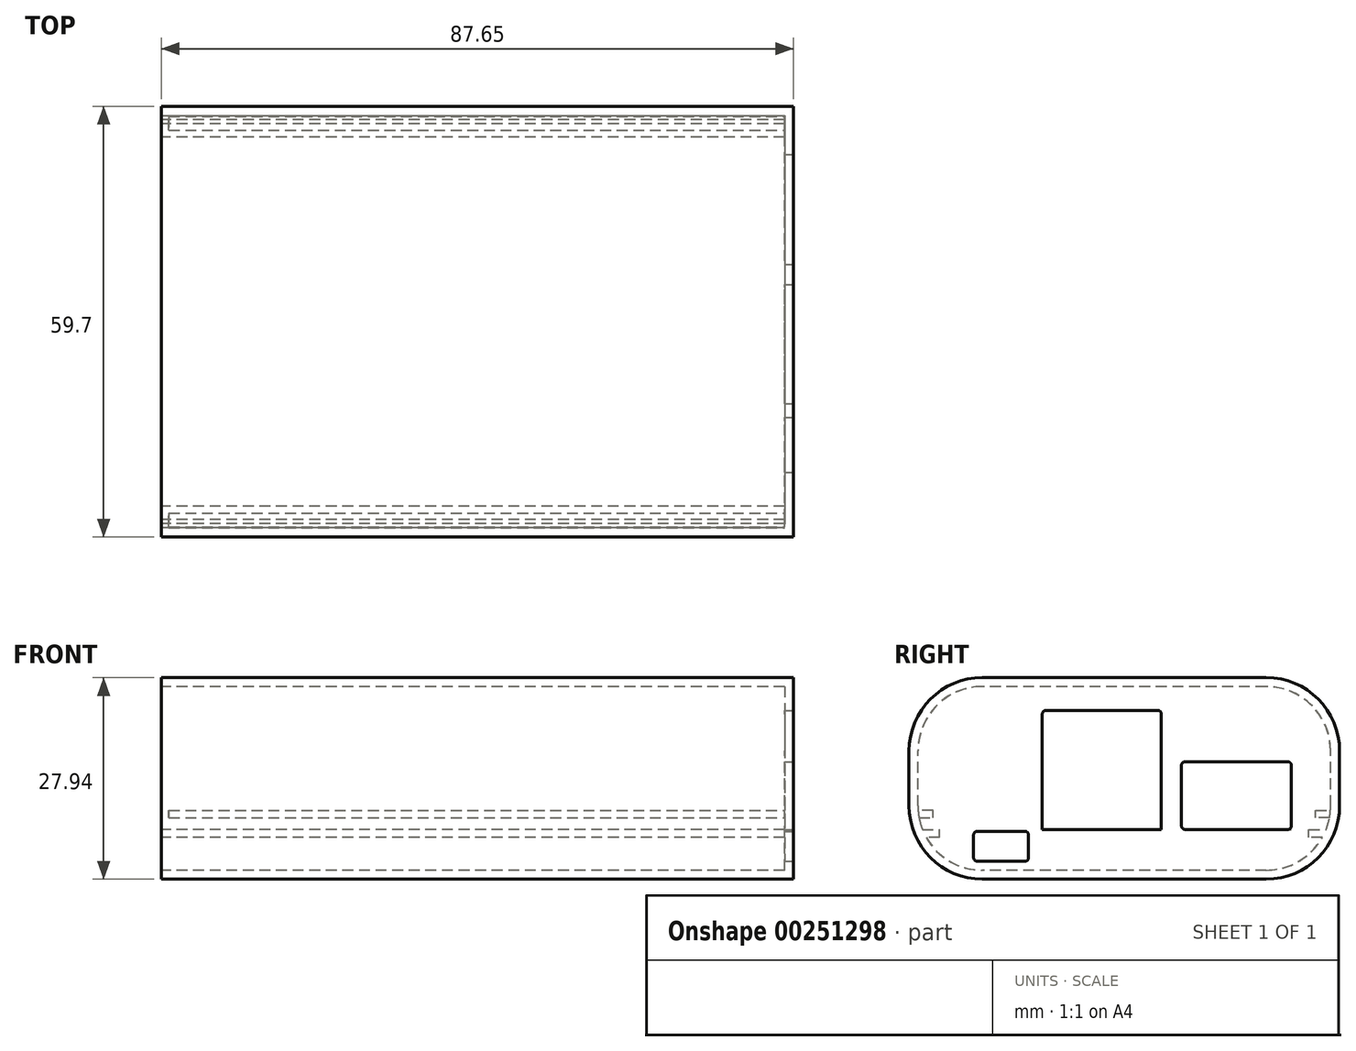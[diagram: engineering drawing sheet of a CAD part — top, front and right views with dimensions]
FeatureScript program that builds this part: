
annotation { "Feature Type Name" : "Feature", "Feature Type Description" : "" }
export const myFeature = defineFeature(function(context is Context, id is Id, definition is map)
    precondition{}
    {
        {
            var Q0;
            Q0=qCreatedBy(makeId("Right.planeOp"),FACE);
            var sketch = newSketch(context, id + "F0", { "sketchPlane" : qUnion([Q0])});
            skLineSegment(sketch, "E0.bottom", {"start": v(19.69, -13.97) * mm, "end": v(-19.69, -13.97) * mm});
            skLineSegment(sketch, "E0.top", {"start": v(19.69, 13.97) * mm, "end": v(-19.69, 13.97) * mm});
            skLineSegment(sketch, "E0.left", {"start": v(29.85, -3.81) * mm, "end": v(29.85, 3.81) * mm});
            skLineSegment(sketch, "E0.right", {"start": v(-29.85, -3.81) * mm, "end": v(-29.85, 3.8) * mm});
            skPoint(sketch, "E0.middle", {"position": v(0, 0) * mm});
            skPoint(sketch, "E1.visualSharp", {"position": v(-29.85, 13.97) * mm});
            skArc(sketch, "E1.filletArc", {"start": v(-19.69, 13.97) * mm, "mid": v(-26.87, 11) * mm, "end": v(-29.85, 3.8) * mm});
            skPoint(sketch, "E2.visualSharp", {"position": v(-29.84, -13.97) * mm});
            skArc(sketch, "E2.filletArc", {"start": v(-29.85, -3.81) * mm, "mid": v(-26.87, -11) * mm, "end": v(-19.69, -13.97) * mm});
            skPoint(sketch, "E3.visualSharp", {"position": v(29.85, -13.97) * mm});
            skArc(sketch, "E3.filletArc", {"start": v(19.69, -13.97) * mm, "mid": v(26.87, -11) * mm, "end": v(29.85, -3.81) * mm});
            skPoint(sketch, "E4.visualSharp", {"position": v(29.85, 13.97) * mm});
            skArc(sketch, "E4.filletArc", {"start": v(29.85, 3.81) * mm, "mid": v(26.87, 11) * mm, "end": v(19.69, 13.97) * mm});
            skSolve(sketch);
        }
        {
            var Q0;
            Q0=makeQuery(id+"F0.imprint","IMPRINT",FACE,{"disambiguationData":[TD([[makeQuery(id+"F0.imprint","IMPRINT",EDGE,{"derivedFrom":sQuery(id+"F0.wireOp",EDGE,"E0.bottom")}),-1.0]])]});
            extrude(context, id + "F1", {"entities" : qUnion([Q0]), "depth" : 44.45 * mm, "hasSecondDirection" : true, "secondDirectionOppositeDirection" : true, "secondDirectionDepth" : 44.45 * mm});
        }
        {
            var Q0;
            Q0=makeQuery(id+"F1.opExtrude","CAP_FACE",FACE,{"disambiguationData":[OSD([sQuery(id+"F0.wireOp",EDGE,"E0.bottom"),sQuery(id+"F0.wireOp",EDGE,"E0.top"),sQuery(id+"F0.wireOp",EDGE,"E0.left"),sQuery(id+"F0.wireOp",EDGE,"E0.right"),sQuery(id+"F0.wireOp",EDGE,"E1.filletArc"),sQuery(id+"F0.wireOp",EDGE,"E2.filletArc"),sQuery(id+"F0.wireOp",EDGE,"E3.filletArc"),sQuery(id+"F0.wireOp",EDGE,"E4.filletArc")])],"isStart":false});
            var Q1;
            Q1=makeQuery(id+"F1.opExtrude","SWEPT_BODY",BODY,{"disambiguationData":[OSD([sQuery(id+"F0.wireOp",EDGE,"E0.bottom"),sQuery(id+"F0.wireOp",EDGE,"E0.top"),sQuery(id+"F0.wireOp",EDGE,"E0.left"),sQuery(id+"F0.wireOp",EDGE,"E0.right"),sQuery(id+"F0.wireOp",EDGE,"E1.filletArc"),sQuery(id+"F0.wireOp",EDGE,"E2.filletArc"),sQuery(id+"F0.wireOp",EDGE,"E3.filletArc"),sQuery(id+"F0.wireOp",EDGE,"E4.filletArc")])]});
            shell(context, id + "F2", {"isHollow" : true, "entities" : qUnion([Q0]), "parts" : qUnion([Q1]), "thickness" : 1.24 * mm});
        }
        {
            var Q0;
            Q0=makeQuery(id+"F1.opExtrude","CAP_FACE",FACE,{"disambiguationData":[OSD([sQuery(id+"F0.wireOp",EDGE,"E0.bottom"),sQuery(id+"F0.wireOp",EDGE,"E0.top"),sQuery(id+"F0.wireOp",EDGE,"E0.left"),sQuery(id+"F0.wireOp",EDGE,"E0.right"),sQuery(id+"F0.wireOp",EDGE,"E1.filletArc"),sQuery(id+"F0.wireOp",EDGE,"E2.filletArc"),sQuery(id+"F0.wireOp",EDGE,"E3.filletArc"),sQuery(id+"F0.wireOp",EDGE,"E4.filletArc")])],"isStart":false});
            var sketch = newSketch(context, id + "F3", { "sketchPlane" : qUnion([Q0])});
            skLineSegment(sketch, "E5", {"start": v(-29.3, -7.09) * mm, "end": v(29.3, -7.09) * mm});
            skLineSegment(sketch, "E6", {"start": v(29.3, -7.09) * mm, "end": v(28.86, -8.18) * mm});
            skLineSegment(sketch, "E7", {"start": v(28.86, -8.18) * mm, "end": v(-28.86, -8.18) * mm});
            skLineSegment(sketch, "E8", {"start": v(-28.86, -8.18) * mm, "end": v(-29.3, -7.09) * mm});
            skSolve(sketch);
        }
        {
            var Q0;
            Q0=makeQuery(id+"F3.imprint","IMPRINT",FACE,{"disambiguationData":[TD([[makeQuery(id+"F3.imprint","IMPRINT",EDGE,{"derivedFrom":sQuery(id+"F3.wireOp",EDGE,"E5")}),-1.0]])]});
            extrude(context, id + "F4", {"entities" : qUnion([Q0]), "operationType" : NewBodyOperationType.ADD, "oppositeDirection" : true, "depth" : 89.36 * mm});
        }
        {
            var Q0;
            Q0=makeQuery(id+"F4.opExtrude","CAP_FACE",FACE,{"disambiguationData":[OSD([sQuery(id+"F3.wireOp",EDGE,"E5"),sQuery(id+"F3.wireOp",EDGE,"E6"),sQuery(id+"F3.wireOp",EDGE,"E7"),sQuery(id+"F3.wireOp",EDGE,"E8")])],"isStart":false});
            var sketch = newSketch(context, id + "F5", { "sketchPlane" : qUnion([Q0])});
            skLineSegment(sketch, "E9", {"start": v(-25.59, -7.09) * mm, "end": v(-25.59, -8.18) * mm});
            skLineSegment(sketch, "E10.MirrorCS", {"start": v(25.59, -7.09) * mm, "end": v(25.59, -8.18) * mm});
            skSolve(sketch);
        }
        {
            var Q0;
            {var subQ0=sQuery(id+"F5.wireOp",EDGE,"E9");Q0=makeQuery(id+"F5.imprint","IMPRINT",FACE,{"disambiguationData":[TD([[makeQuery(id+"F5.imprint","IMPRINT",EDGE,{"derivedFrom":subQ0}),1.0]])]});}
            extrude(context, id + "F6", {"entities" : qUnion([Q0]), "operationType" : NewBodyOperationType.REMOVE, "oppositeDirection" : true, "depth" : 89.4 * mm});
        }
        {
            var Q0;
            Q0=makeQuery(id+"F1.opExtrude","CAP_FACE",FACE,{"disambiguationData":[OSD([sQuery(id+"F0.wireOp",EDGE,"E0.bottom"),sQuery(id+"F0.wireOp",EDGE,"E0.top"),sQuery(id+"F0.wireOp",EDGE,"E0.left"),sQuery(id+"F0.wireOp",EDGE,"E0.right"),sQuery(id+"F0.wireOp",EDGE,"E1.filletArc"),sQuery(id+"F0.wireOp",EDGE,"E2.filletArc"),sQuery(id+"F0.wireOp",EDGE,"E3.filletArc"),sQuery(id+"F0.wireOp",EDGE,"E4.filletArc")])],"isStart":false});
            var sketch = newSketch(context, id + "F7", { "sketchPlane" : qUnion([Q0])});
            skLineSegment(sketch, "E11", {"start": v(-11.36, -7.09) * mm, "end": v(-11.36, 9.42) * mm});
            skLineSegment(sketch, "E12", {"start": v(-11.36, 9.42) * mm, "end": v(5.15, 9.42) * mm});
            skLineSegment(sketch, "E13", {"start": v(5.15, 9.42) * mm, "end": v(5.15, -7.09) * mm});
            skLineSegment(sketch, "E14", {"start": v(7.93, -7.09) * mm, "end": v(7.93, 2.31) * mm});
            skLineSegment(sketch, "E15", {"start": v(7.93, 2.31) * mm, "end": v(23.17, 2.31) * mm});
            skLineSegment(sketch, "E16", {"start": v(23.17, 2.31) * mm, "end": v(23.17, -7.09) * mm});
            skSolve(sketch);
        }
        {
            var Q0;
            {var subQ0=sQuery(id+"F7.wireOp",EDGE,"E11");Q0=makeQuery(id+"F7.imprint","IMPRINT",FACE,{"disambiguationData":[TD([[makeQuery(id+"F7.imprint","IMPRINT",EDGE,{"derivedFrom":subQ0}),-1.0]])]});}
            var Q1;
            {var subQ0=sQuery(id+"F7.wireOp",EDGE,"E14");Q1=makeQuery(id+"F7.imprint","IMPRINT",FACE,{"disambiguationData":[TD([[makeQuery(id+"F7.imprint","IMPRINT",EDGE,{"derivedFrom":subQ0}),-1.0]])]});}
            extrude(context, id + "F8", {"entities" : qUnion([Q0, Q1]), "operationType" : NewBodyOperationType.REMOVE, "oppositeDirection" : true, "depth" : 25.4 * mm});
        }
        {
            var Q0;
            Q0=makeQuery(id+"F1.opExtrude","CAP_FACE",FACE,{"disambiguationData":[OSD([sQuery(id+"F0.wireOp",EDGE,"E0.bottom"),sQuery(id+"F0.wireOp",EDGE,"E0.top"),sQuery(id+"F0.wireOp",EDGE,"E0.left"),sQuery(id+"F0.wireOp",EDGE,"E0.right"),sQuery(id+"F0.wireOp",EDGE,"E1.filletArc"),sQuery(id+"F0.wireOp",EDGE,"E2.filletArc"),sQuery(id+"F0.wireOp",EDGE,"E3.filletArc"),sQuery(id+"F0.wireOp",EDGE,"E4.filletArc")])],"isStart":false});
            var sketch = newSketch(context, id + "F9", { "sketchPlane" : qUnion([Q0])});
            skLineSegment(sketch, "E17", {"start": v(-13.27, -8.18) * mm, "end": v(-13.27, -11.48) * mm});
            skLineSegment(sketch, "E18", {"start": v(-13.27, -11.48) * mm, "end": v(-20.89, -11.48) * mm});
            skLineSegment(sketch, "E19", {"start": v(-20.89, -11.48) * mm, "end": v(-20.89, -8.18) * mm});
            skSolve(sketch);
        }
        {
            var Q0;
            {var subQ0=sQuery(id+"F9.wireOp",EDGE,"E17");Q0=makeQuery(id+"F9.imprint","IMPRINT",FACE,{"disambiguationData":[TD([[makeQuery(id+"F9.imprint","IMPRINT",EDGE,{"derivedFrom":subQ0}),-1.0]])]});}
            extrude(context, id + "F10", {"entities" : qUnion([Q0]), "operationType" : NewBodyOperationType.REMOVE, "oppositeDirection" : true, "depth" : 25.4 * mm});
        }
        {
            var Q0;
            Q0=makeQuery(id+"F1.opExtrude","CAP_FACE",FACE,{"disambiguationData":[OSD([sQuery(id+"F0.wireOp",EDGE,"E0.bottom"),sQuery(id+"F0.wireOp",EDGE,"E0.top"),sQuery(id+"F0.wireOp",EDGE,"E0.left"),sQuery(id+"F0.wireOp",EDGE,"E0.right"),sQuery(id+"F0.wireOp",EDGE,"E1.filletArc"),sQuery(id+"F0.wireOp",EDGE,"E2.filletArc"),sQuery(id+"F0.wireOp",EDGE,"E3.filletArc"),sQuery(id+"F0.wireOp",EDGE,"E4.filletArc")])],"isStart":false});
            var sketch = newSketch(context, id + "F11", { "sketchPlane" : qUnion([Q0])});
            skLineSegment(sketch, "E20", {"start": v(-11.36, -7.09) * mm, "end": v(5.15, -7.09) * mm});
            skLineSegment(sketch, "E21", {"start": v(5.15, -7.09) * mm, "end": v(7.93, -7.09) * mm});
            skLineSegment(sketch, "E22", {"start": v(7.93, -7.09) * mm, "end": v(23.17, -7.09) * mm});
            skLineSegment(sketch, "E23", {"start": v(-20.89, -8.18) * mm, "end": v(-13.27, -8.18) * mm});
            skSolve(sketch);
        }
        {
            var Q0;
            Q0=makeQuery(id+"F11.imprint","IMPRINT",FACE,{"disambiguationData":[TD([[makeQuery(id+"F11.imprint","IMPRINT",EDGE,{"derivedFrom":sQuery(id+"F11.wireOp",EDGE,"E20")}),-1.0]])]});
            extrude(context, id + "F12", {"entities" : qUnion([Q0]), "operationType" : NewBodyOperationType.ADD, "oppositeDirection" : true, "depth" : 1.25 * mm});
        }
        {
            var Q0;
            {var subQ0=sQuery(id+"F0.wireOp",EDGE,"E4.filletArc");var subQ1=sQuery(id+"F0.wireOp",EDGE,"E2.filletArc");var subQ2=sQuery(id+"F0.wireOp",EDGE,"E1.filletArc");var subQ3=sQuery(id+"F0.wireOp",EDGE,"E3.filletArc");var subQ4=sQuery(id+"F0.wireOp",EDGE,"E0.right");var subQ5=sQuery(id+"F0.wireOp",EDGE,"E0.left");var subQ6=sQuery(id+"F0.wireOp",EDGE,"E0.top");var subQ7=makeQuery(id+"F1.opExtrude","CAP_FACE",FACE,{"disambiguationData":[OSD([sQuery(id+"F0.wireOp",EDGE,"E0.bottom"),subQ6,subQ5,subQ4,subQ2,subQ1,subQ3,subQ0])],"isStart":true});Q0=makeQuery(id+"F4.boolean.opBoolean","SPLIT",FACE,{"disambiguationData":[TD([subQ7,makeQuery(id+"F1.opExtrude","SWEPT_FACE",FACE,{"disambiguationData":[OSD([subQ6])]}),makeQuery(id+"F1.opExtrude","SWEPT_FACE",FACE,{"disambiguationData":[OSD([subQ5])]}),makeQuery(id+"F1.opExtrude","SWEPT_FACE",FACE,{"disambiguationData":[OSD([subQ4])]}),makeQuery(id+"F1.opExtrude","SWEPT_FACE",FACE,{"disambiguationData":[OSD([subQ2])]}),makeQuery(id+"F1.opExtrude","SWEPT_FACE",FACE,{"disambiguationData":[OSD([subQ1])]}),makeQuery(id+"F1.opExtrude","SWEPT_FACE",FACE,{"disambiguationData":[OSD([subQ3])]}),makeQuery(id+"F1.opExtrude","SWEPT_FACE",FACE,{"disambiguationData":[OSD([subQ0])]}),makeQuery(id+"F4.opExtrude","SWEPT_FACE",FACE,{"disambiguationData":[OSD([sQuery(id+"F3.wireOp",EDGE,"E5")])]}),makeQuery(id+"F4.opExtrude","SWEPT_FACE",FACE,{"disambiguationData":[OSD([sQuery(id+"F3.wireOp",EDGE,"E6")])]}),makeQuery(id+"F4.opExtrude","SWEPT_FACE",FACE,{"disambiguationData":[OSD([sQuery(id+"F3.wireOp",EDGE,"E8")])]})])],"derivedFrom":subQ7});}
            var Q1;
            {var subQ0=sQuery(id+"F0.wireOp",EDGE,"E3.filletArc");var subQ1=sQuery(id+"F0.wireOp",EDGE,"E2.filletArc");var subQ2=sQuery(id+"F0.wireOp",EDGE,"E0.bottom");var subQ3=makeQuery(id+"F1.opExtrude","CAP_FACE",FACE,{"disambiguationData":[OSD([subQ2,sQuery(id+"F0.wireOp",EDGE,"E0.top"),sQuery(id+"F0.wireOp",EDGE,"E0.left"),sQuery(id+"F0.wireOp",EDGE,"E0.right"),sQuery(id+"F0.wireOp",EDGE,"E1.filletArc"),subQ1,subQ0,sQuery(id+"F0.wireOp",EDGE,"E4.filletArc")])],"isStart":true});Q1=makeQuery(id+"F4.boolean.opBoolean","SPLIT",FACE,{"disambiguationData":[TD([makeQuery(id+"F1.opExtrude","SWEPT_FACE",FACE,{"disambiguationData":[OSD([subQ2])]}),subQ3,makeQuery(id+"F1.opExtrude","SWEPT_FACE",FACE,{"disambiguationData":[OSD([subQ1])]}),makeQuery(id+"F1.opExtrude","SWEPT_FACE",FACE,{"disambiguationData":[OSD([subQ0])]}),makeQuery(id+"F4.opExtrude","SWEPT_FACE",FACE,{"disambiguationData":[OSD([sQuery(id+"F3.wireOp",EDGE,"E6")])]}),makeQuery(id+"F4.opExtrude","SWEPT_FACE",FACE,{"disambiguationData":[OSD([sQuery(id+"F3.wireOp",EDGE,"E7")])]}),makeQuery(id+"F4.opExtrude","SWEPT_FACE",FACE,{"disambiguationData":[OSD([sQuery(id+"F3.wireOp",EDGE,"E8")])]})])],"derivedFrom":subQ3});}
            extrude(context, id + "F13", {"entities" : qUnion([Q0, Q1]), "operationType" : NewBodyOperationType.REMOVE, "oppositeDirection" : true, "depth" : 1.25 * mm});
        }
        {
            var Q0;
            {var subQ0=sQuery(id+"F3.wireOp",EDGE,"E5");var subQ1=sQuery(id+"F3.wireOp",EDGE,"E6");var subQ2=sQuery(id+"F3.wireOp",EDGE,"E7");Q0=makeQuery(id+"F6.boolean.opBoolean","SPLIT",FACE,{"disambiguationData":[TD([makeQuery(id+"F4.opExtrude","SWEPT_FACE",FACE,{"disambiguationData":[OSD([subQ1])]})])],"derivedFrom":makeQuery(id+"F4.opExtrude","CAP_FACE",FACE,{"disambiguationData":[OSD([subQ0,subQ1,subQ2,sQuery(id+"F3.wireOp",EDGE,"E8")])],"isStart":false})});}
            var Q1;
            {var subQ0=sQuery(id+"F3.wireOp",EDGE,"E5");var subQ1=sQuery(id+"F3.wireOp",EDGE,"E8");var subQ2=sQuery(id+"F3.wireOp",EDGE,"E7");Q1=makeQuery(id+"F6.boolean.opBoolean","SPLIT",FACE,{"disambiguationData":[TD([makeQuery(id+"F4.opExtrude","SWEPT_FACE",FACE,{"disambiguationData":[OSD([subQ1])]})])],"derivedFrom":makeQuery(id+"F4.opExtrude","CAP_FACE",FACE,{"disambiguationData":[OSD([subQ0,sQuery(id+"F3.wireOp",EDGE,"E6"),subQ2,subQ1])],"isStart":false})});}
            var Q2;
            {var subQ0=sQuery(id+"F0.wireOp",EDGE,"E2.filletArc");var subQ1=makeQuery(id+"F1.opExtrude","CAP_FACE",FACE,{"disambiguationData":[OSD([sQuery(id+"F0.wireOp",EDGE,"E0.bottom"),sQuery(id+"F0.wireOp",EDGE,"E0.top"),sQuery(id+"F0.wireOp",EDGE,"E0.left"),sQuery(id+"F0.wireOp",EDGE,"E0.right"),sQuery(id+"F0.wireOp",EDGE,"E1.filletArc"),subQ0,sQuery(id+"F0.wireOp",EDGE,"E3.filletArc"),sQuery(id+"F0.wireOp",EDGE,"E4.filletArc")])],"isStart":true});Q2=makeQuery(id+"F4.boolean.opBoolean","SPLIT",FACE,{"disambiguationData":[TD([subQ1,makeQuery(id+"F1.opExtrude","SWEPT_FACE",FACE,{"disambiguationData":[OSD([subQ0])]}),makeQuery(id+"F4.opExtrude","SWEPT_FACE",FACE,{"disambiguationData":[OSD([sQuery(id+"F3.wireOp",EDGE,"E5")])]}),makeQuery(id+"F4.opExtrude","SWEPT_FACE",FACE,{"disambiguationData":[OSD([sQuery(id+"F3.wireOp",EDGE,"E7")])]}),makeQuery(id+"F4.opExtrude","SWEPT_FACE",FACE,{"disambiguationData":[OSD([sQuery(id+"F3.wireOp",EDGE,"E8")])]})])],"derivedFrom":subQ1});}
            var Q3;
            {var subQ0=sQuery(id+"F0.wireOp",EDGE,"E3.filletArc");var subQ1=makeQuery(id+"F1.opExtrude","CAP_FACE",FACE,{"disambiguationData":[OSD([sQuery(id+"F0.wireOp",EDGE,"E0.bottom"),sQuery(id+"F0.wireOp",EDGE,"E0.top"),sQuery(id+"F0.wireOp",EDGE,"E0.left"),sQuery(id+"F0.wireOp",EDGE,"E0.right"),sQuery(id+"F0.wireOp",EDGE,"E1.filletArc"),sQuery(id+"F0.wireOp",EDGE,"E2.filletArc"),subQ0,sQuery(id+"F0.wireOp",EDGE,"E4.filletArc")])],"isStart":true});Q3=makeQuery(id+"F4.boolean.opBoolean","SPLIT",FACE,{"disambiguationData":[TD([subQ1,makeQuery(id+"F1.opExtrude","SWEPT_FACE",FACE,{"disambiguationData":[OSD([subQ0])]}),makeQuery(id+"F4.opExtrude","SWEPT_FACE",FACE,{"disambiguationData":[OSD([sQuery(id+"F3.wireOp",EDGE,"E5")])]}),makeQuery(id+"F4.opExtrude","SWEPT_FACE",FACE,{"disambiguationData":[OSD([sQuery(id+"F3.wireOp",EDGE,"E6")])]}),makeQuery(id+"F4.opExtrude","SWEPT_FACE",FACE,{"disambiguationData":[OSD([sQuery(id+"F3.wireOp",EDGE,"E7")])]})])],"derivedFrom":subQ1});}
            extrude(context, id + "F14", {"entities" : qUnion([Q0, Q1, Q2, Q3]), "operationType" : NewBodyOperationType.REMOVE, "oppositeDirection" : true, "depth" : 1.7 * mm});
        }
        {
            var Q0;
            {var subQ0=sQuery(id+"F0.wireOp",EDGE,"E3.filletArc");var subQ1=sQuery(id+"F0.wireOp",EDGE,"E4.filletArc");var subQ2=sQuery(id+"F0.wireOp",EDGE,"E2.filletArc");var subQ3=sQuery(id+"F0.wireOp",EDGE,"E1.filletArc");var subQ4=sQuery(id+"F0.wireOp",EDGE,"E0.right");var subQ5=sQuery(id+"F0.wireOp",EDGE,"E0.left");var subQ6=sQuery(id+"F0.wireOp",EDGE,"E0.top");var subQ7=sQuery(id+"F0.wireOp",EDGE,"E0.bottom");var subQ8=makeQuery(id+"F1.opExtrude","CAP_FACE",FACE,{"disambiguationData":[OSD([subQ7,subQ6,subQ5,subQ4,subQ3,subQ2,subQ0,subQ1])],"isStart":true});Q0=makeQuery(id+"F14.boolean.opBoolean","COPY",FACE,{"derivedFrom":makeQuery(id+"F14.opExtrude","CAP_FACE",FACE,{"disambiguationData":[OSD([subQ7,subQ6,subQ5,subQ4,subQ3,subQ2,subQ0,subQ1]),TDD([makeQuery(id+"F4.boolean.opBoolean","SPLIT",FACE,{"disambiguationData":[TD([subQ8,makeQuery(id+"F1.opExtrude","SWEPT_FACE",FACE,{"disambiguationData":[OSD([subQ0])]}),makeQuery(id+"F4.opExtrude","SWEPT_FACE",FACE,{"disambiguationData":[OSD([sQuery(id+"F3.wireOp",EDGE,"E5")])]}),makeQuery(id+"F4.opExtrude","SWEPT_FACE",FACE,{"disambiguationData":[OSD([sQuery(id+"F3.wireOp",EDGE,"E6")])]}),makeQuery(id+"F4.opExtrude","SWEPT_FACE",FACE,{"disambiguationData":[OSD([sQuery(id+"F3.wireOp",EDGE,"E7")])]})])],"derivedFrom":subQ8})])],"isStart":false})});}
            var Q1;
            {var subQ0=sQuery(id+"F0.wireOp",EDGE,"E2.filletArc");var subQ1=sQuery(id+"F0.wireOp",EDGE,"E4.filletArc");var subQ2=sQuery(id+"F0.wireOp",EDGE,"E3.filletArc");var subQ3=sQuery(id+"F0.wireOp",EDGE,"E1.filletArc");var subQ4=sQuery(id+"F0.wireOp",EDGE,"E0.right");var subQ5=sQuery(id+"F0.wireOp",EDGE,"E0.left");var subQ6=sQuery(id+"F0.wireOp",EDGE,"E0.top");var subQ7=sQuery(id+"F0.wireOp",EDGE,"E0.bottom");var subQ8=makeQuery(id+"F1.opExtrude","CAP_FACE",FACE,{"disambiguationData":[OSD([subQ7,subQ6,subQ5,subQ4,subQ3,subQ0,subQ2,subQ1])],"isStart":true});Q1=makeQuery(id+"F14.boolean.opBoolean","COPY",FACE,{"derivedFrom":makeQuery(id+"F14.opExtrude","CAP_FACE",FACE,{"disambiguationData":[OSD([subQ7,subQ6,subQ5,subQ4,subQ3,subQ0,subQ2,subQ1]),TDD([makeQuery(id+"F4.boolean.opBoolean","SPLIT",FACE,{"disambiguationData":[TD([subQ8,makeQuery(id+"F1.opExtrude","SWEPT_FACE",FACE,{"disambiguationData":[OSD([subQ0])]}),makeQuery(id+"F4.opExtrude","SWEPT_FACE",FACE,{"disambiguationData":[OSD([sQuery(id+"F3.wireOp",EDGE,"E5")])]}),makeQuery(id+"F4.opExtrude","SWEPT_FACE",FACE,{"disambiguationData":[OSD([sQuery(id+"F3.wireOp",EDGE,"E7")])]}),makeQuery(id+"F4.opExtrude","SWEPT_FACE",FACE,{"disambiguationData":[OSD([sQuery(id+"F3.wireOp",EDGE,"E8")])]})])],"derivedFrom":subQ8})])],"isStart":false})});}
            extrude(context, id + "F15", {"entities" : qUnion([Q0, Q1]), "operationType" : NewBodyOperationType.ADD, "depth" : 0.46 * mm});
        }
        {
            var Q0;
            {var subQ0=sQuery(id+"F0.wireOp",EDGE,"E4.filletArc");var subQ1=sQuery(id+"F0.wireOp",EDGE,"E3.filletArc");var subQ2=sQuery(id+"F0.wireOp",EDGE,"E2.filletArc");var subQ3=sQuery(id+"F0.wireOp",EDGE,"E1.filletArc");var subQ4=sQuery(id+"F0.wireOp",EDGE,"E0.right");var subQ5=sQuery(id+"F0.wireOp",EDGE,"E0.left");var subQ6=sQuery(id+"F0.wireOp",EDGE,"E0.top");var subQ7=sQuery(id+"F0.wireOp",EDGE,"E0.bottom");Q0=makeQuery(id+"F12.boolean.opBoolean","MERGE",FACE,{"derivedFrom":[makeQuery(id+"F1.opExtrude","CAP_FACE",FACE,{"disambiguationData":[OSD([subQ7,subQ6,subQ5,subQ4,subQ3,subQ2,subQ1,subQ0])],"isStart":false}),makeQuery(id+"F12.opExtrude","CAP_FACE",FACE,{"disambiguationData":[OSD([subQ7,subQ6,subQ5,subQ4,subQ3,subQ2,subQ1,subQ0,sQuery(id+"F3.wireOp",EDGE,"E5"),sQuery(id+"F3.wireOp",EDGE,"E7"),sQuery(id+"F5.wireOp",EDGE,"E9"),sQuery(id+"F5.wireOp",EDGE,"E10.MirrorCS"),sQuery(id+"F11.wireOp",EDGE,"E20"),sQuery(id+"F11.wireOp",EDGE,"E21"),sQuery(id+"F11.wireOp",EDGE,"E22"),sQuery(id+"F11.wireOp",EDGE,"E23")])],"isStart":true})]});}
            var sketch = newSketch(context, id + "F16", { "sketchPlane" : qUnion([Q0])});
            skLineSegment(sketch, "E24", {"start": v(-20.89, -8.18) * mm, "end": v(-20.89, -7.34) * mm});
            skLineSegment(sketch, "E25", {"start": v(-20.89, -7.34) * mm, "end": v(-13.27, -7.34) * mm});
            skLineSegment(sketch, "E26", {"start": v(-13.27, -7.34) * mm, "end": v(-13.27, -8.18) * mm});
            skLineSegment(sketch, "E27", {"start": v(-13.27, -8.18) * mm, "end": v(-20.89, -8.18) * mm});
            skSolve(sketch);
        }
        {
            var Q0;
            Q0=makeQuery(id+"F16.imprint","IMPRINT",FACE,{"disambiguationData":[TD([[makeQuery(id+"F16.imprint","IMPRINT",EDGE,{"derivedFrom":sQuery(id+"F16.wireOp",EDGE,"E24")}),-1.0]])]});
            extrude(context, id + "F17", {"entities" : qUnion([Q0]), "operationType" : NewBodyOperationType.REMOVE, "oppositeDirection" : true, "depth" : 25.4 * mm});
        }
        {
            var Q0;
            Q0=makeQuery(id+"F10.boolean.opBoolean","COPY",EDGE,{"derivedFrom":makeQuery(id+"F10.opExtrude","SWEPT_EDGE",EDGE,{"disambiguationData":[OSD([sQuery(id+"F9.wireOp",EDGE,"E17"),sQuery(id+"F9.wireOp",EDGE,"E18")])]})});
            var Q1;
            Q1=makeQuery(id+"F10.boolean.opBoolean","COPY",EDGE,{"derivedFrom":makeQuery(id+"F10.opExtrude","SWEPT_EDGE",EDGE,{"disambiguationData":[OSD([sQuery(id+"F9.wireOp",EDGE,"E18"),sQuery(id+"F9.wireOp",EDGE,"E19")])]})});
            var Q2;
            Q2=makeQuery(id+"F10.boolean.opBoolean","COPY",EDGE,{"derivedFrom":makeQuery(id+"F10.opExtrude","SWEPT_EDGE",EDGE,{"disambiguationData":[OSD([sQuery(id+"F0.wireOp",EDGE,"E0.bottom"),sQuery(id+"F0.wireOp",EDGE,"E0.top"),sQuery(id+"F0.wireOp",EDGE,"E0.left"),sQuery(id+"F0.wireOp",EDGE,"E0.right"),sQuery(id+"F0.wireOp",EDGE,"E1.filletArc"),sQuery(id+"F0.wireOp",EDGE,"E2.filletArc"),sQuery(id+"F0.wireOp",EDGE,"E3.filletArc"),sQuery(id+"F0.wireOp",EDGE,"E4.filletArc"),sQuery(id+"F3.wireOp",EDGE,"E7"),sQuery(id+"F9.wireOp",EDGE,"E17")])]})});
            var Q3;
            Q3=makeQuery(id+"F10.boolean.opBoolean","COPY",EDGE,{"derivedFrom":makeQuery(id+"F10.opExtrude","SWEPT_EDGE",EDGE,{"disambiguationData":[OSD([sQuery(id+"F0.wireOp",EDGE,"E0.bottom"),sQuery(id+"F0.wireOp",EDGE,"E0.top"),sQuery(id+"F0.wireOp",EDGE,"E0.left"),sQuery(id+"F0.wireOp",EDGE,"E0.right"),sQuery(id+"F0.wireOp",EDGE,"E1.filletArc"),sQuery(id+"F0.wireOp",EDGE,"E2.filletArc"),sQuery(id+"F0.wireOp",EDGE,"E3.filletArc"),sQuery(id+"F0.wireOp",EDGE,"E4.filletArc"),sQuery(id+"F3.wireOp",EDGE,"E7"),sQuery(id+"F9.wireOp",EDGE,"E19")])]})});
            var Q4;
            Q4=makeQuery(id+"F8.boolean.opBoolean","COPY",EDGE,{"derivedFrom":makeQuery(id+"F8.opExtrude","SWEPT_EDGE",EDGE,{"disambiguationData":[OSD([sQuery(id+"F7.wireOp",EDGE,"E12"),sQuery(id+"F7.wireOp",EDGE,"E13")])]})});
            var Q5;
            Q5=makeQuery(id+"F8.boolean.opBoolean","COPY",EDGE,{"derivedFrom":makeQuery(id+"F8.opExtrude","SWEPT_EDGE",EDGE,{"disambiguationData":[OSD([sQuery(id+"F7.wireOp",EDGE,"E11"),sQuery(id+"F7.wireOp",EDGE,"E12")])]})});
            var Q6;
            Q6=makeQuery(id+"F8.boolean.opBoolean","COPY",EDGE,{"derivedFrom":makeQuery(id+"F8.opExtrude","SWEPT_EDGE",EDGE,{"disambiguationData":[OSD([sQuery(id+"F0.wireOp",EDGE,"E0.bottom"),sQuery(id+"F0.wireOp",EDGE,"E0.top"),sQuery(id+"F0.wireOp",EDGE,"E0.left"),sQuery(id+"F0.wireOp",EDGE,"E0.right"),sQuery(id+"F0.wireOp",EDGE,"E1.filletArc"),sQuery(id+"F0.wireOp",EDGE,"E2.filletArc"),sQuery(id+"F0.wireOp",EDGE,"E3.filletArc"),sQuery(id+"F0.wireOp",EDGE,"E4.filletArc"),sQuery(id+"F3.wireOp",EDGE,"E5"),sQuery(id+"F7.wireOp",EDGE,"E13")])]})});
            var Q7;
            Q7=makeQuery(id+"F8.boolean.opBoolean","COPY",EDGE,{"derivedFrom":makeQuery(id+"F8.opExtrude","SWEPT_EDGE",EDGE,{"disambiguationData":[OSD([sQuery(id+"F0.wireOp",EDGE,"E0.bottom"),sQuery(id+"F0.wireOp",EDGE,"E0.top"),sQuery(id+"F0.wireOp",EDGE,"E0.left"),sQuery(id+"F0.wireOp",EDGE,"E0.right"),sQuery(id+"F0.wireOp",EDGE,"E1.filletArc"),sQuery(id+"F0.wireOp",EDGE,"E2.filletArc"),sQuery(id+"F0.wireOp",EDGE,"E3.filletArc"),sQuery(id+"F0.wireOp",EDGE,"E4.filletArc"),sQuery(id+"F3.wireOp",EDGE,"E5"),sQuery(id+"F7.wireOp",EDGE,"E11")])]})});
            var Q8;
            Q8=makeQuery(id+"F8.boolean.opBoolean","COPY",EDGE,{"derivedFrom":makeQuery(id+"F8.opExtrude","SWEPT_EDGE",EDGE,{"disambiguationData":[OSD([sQuery(id+"F0.wireOp",EDGE,"E0.bottom"),sQuery(id+"F0.wireOp",EDGE,"E0.top"),sQuery(id+"F0.wireOp",EDGE,"E0.left"),sQuery(id+"F0.wireOp",EDGE,"E0.right"),sQuery(id+"F0.wireOp",EDGE,"E1.filletArc"),sQuery(id+"F0.wireOp",EDGE,"E2.filletArc"),sQuery(id+"F0.wireOp",EDGE,"E3.filletArc"),sQuery(id+"F0.wireOp",EDGE,"E4.filletArc"),sQuery(id+"F3.wireOp",EDGE,"E5"),sQuery(id+"F7.wireOp",EDGE,"E14")])]})});
            var Q9;
            Q9=makeQuery(id+"F8.boolean.opBoolean","COPY",EDGE,{"derivedFrom":makeQuery(id+"F8.opExtrude","SWEPT_EDGE",EDGE,{"disambiguationData":[OSD([sQuery(id+"F7.wireOp",EDGE,"E14"),sQuery(id+"F7.wireOp",EDGE,"E15")])]})});
            var Q10;
            Q10=makeQuery(id+"F8.boolean.opBoolean","COPY",EDGE,{"derivedFrom":makeQuery(id+"F8.opExtrude","SWEPT_EDGE",EDGE,{"disambiguationData":[OSD([sQuery(id+"F0.wireOp",EDGE,"E0.bottom"),sQuery(id+"F0.wireOp",EDGE,"E0.top"),sQuery(id+"F0.wireOp",EDGE,"E0.left"),sQuery(id+"F0.wireOp",EDGE,"E0.right"),sQuery(id+"F0.wireOp",EDGE,"E1.filletArc"),sQuery(id+"F0.wireOp",EDGE,"E2.filletArc"),sQuery(id+"F0.wireOp",EDGE,"E3.filletArc"),sQuery(id+"F0.wireOp",EDGE,"E4.filletArc"),sQuery(id+"F3.wireOp",EDGE,"E5"),sQuery(id+"F7.wireOp",EDGE,"E16")])]})});
            var Q11;
            Q11=makeQuery(id+"F8.boolean.opBoolean","COPY",EDGE,{"derivedFrom":makeQuery(id+"F8.opExtrude","SWEPT_EDGE",EDGE,{"disambiguationData":[OSD([sQuery(id+"F7.wireOp",EDGE,"E15"),sQuery(id+"F7.wireOp",EDGE,"E16")])]})});
            var Q12;
            Q12=makeQuery(id+"F17.boolean.opBoolean","COPY",EDGE,{"derivedFrom":makeQuery(id+"F17.opExtrude","SWEPT_EDGE",EDGE,{"disambiguationData":[OSD([sQuery(id+"F16.wireOp",EDGE,"E24"),sQuery(id+"F16.wireOp",EDGE,"E25")])]})});
            var Q13;
            Q13=makeQuery(id+"F17.boolean.opBoolean","COPY",EDGE,{"derivedFrom":makeQuery(id+"F17.opExtrude","SWEPT_EDGE",EDGE,{"disambiguationData":[OSD([sQuery(id+"F16.wireOp",EDGE,"E25"),sQuery(id+"F16.wireOp",EDGE,"E26")])]})});
            fillet(context, id + "F18", {"entities" : qUnion([Q0, Q1, Q2, Q3, Q4, Q5, Q6, Q7, Q8, Q9, Q10, Q11, Q12, Q13]), "radius" : 0.5 * mm, "tangentPropagation" : true, "allowEdgeOverflow" : false});
        }
        {
            var Q0;
            {var subQ0=sQuery(id+"F0.wireOp",EDGE,"E1.filletArc");var subQ1=sQuery(id+"F0.wireOp",EDGE,"E0.right");var subQ2=sQuery(id+"F0.wireOp",EDGE,"E0.left");var subQ3=sQuery(id+"F0.wireOp",EDGE,"E0.top");var subQ4=sQuery(id+"F0.wireOp",EDGE,"E2.filletArc");var subQ5=sQuery(id+"F0.wireOp",EDGE,"E3.filletArc");var subQ6=sQuery(id+"F0.wireOp",EDGE,"E4.filletArc");var subQ7=sQuery(id+"F0.wireOp",EDGE,"E0.bottom");Q0=makeQuery(id+"F4.boolean.opBoolean","SPLIT",FACE,{"disambiguationData":[TD([makeQuery(id+"F2.opShell","OFFSET_FACE",FACE,{"disambiguationData":[OSD([subQ3])]})])],"derivedFrom":makeQuery(id+"F2.opShell","OFFSET_FACE",FACE,{"disambiguationData":[OSD([subQ7,subQ3,subQ2,subQ1,subQ0,subQ4,subQ5,subQ6]),TDD([makeQuery(id+"F1.opExtrude","CAP_FACE",FACE,{"disambiguationData":[OSD([subQ7,subQ3,subQ2,subQ1,subQ0,subQ4,subQ5,subQ6])],"isStart":false})])]})});}
            var sketch = newSketch(context, id + "F19", { "sketchPlane" : qUnion([Q0])});
            skLineSegment(sketch, "E28", {"start": v(-28.45, -5.44) * mm, "end": v(-26.51, -5.44) * mm});
            skLineSegment(sketch, "E29", {"start": v(-26.51, -5.44) * mm, "end": v(-26.51, -4.42) * mm});
            skLineSegment(sketch, "E30", {"start": v(-26.51, -4.42) * mm, "end": v(-28.58, -4.42) * mm});
            skLineSegment(sketch, "E31.MirrorCS", {"start": v(28.45, -5.44) * mm, "end": v(26.51, -5.44) * mm});
            skLineSegment(sketch, "E32.MirrorCS", {"start": v(26.51, -5.44) * mm, "end": v(26.51, -4.42) * mm});
            skLineSegment(sketch, "E33.MirrorCS", {"start": v(26.51, -4.42) * mm, "end": v(28.58, -4.42) * mm});
            skSolve(sketch);
        }
        {
            var Q0;
            {var subQ0=sQuery(id+"F19.wireOp",EDGE,"E28");Q0=makeQuery(id+"F19.imprint","IMPRINT",FACE,{"disambiguationData":[TD([[makeQuery(id+"F19.imprint","IMPRINT",EDGE,{"derivedFrom":subQ0}),1.0]])]});}
            var Q1;
            {var subQ0=sQuery(id+"F19.wireOp",EDGE,"E31.MirrorCS");Q1=makeQuery(id+"F19.imprint","IMPRINT",FACE,{"disambiguationData":[TD([[makeQuery(id+"F19.imprint","IMPRINT",EDGE,{"derivedFrom":subQ0}),-1.0]])]});}
            extrude(context, id + "F20", {"entities" : qUnion([Q0, Q1]), "operationType" : NewBodyOperationType.ADD, "depth" : 85.37 * mm});
        }
    });
